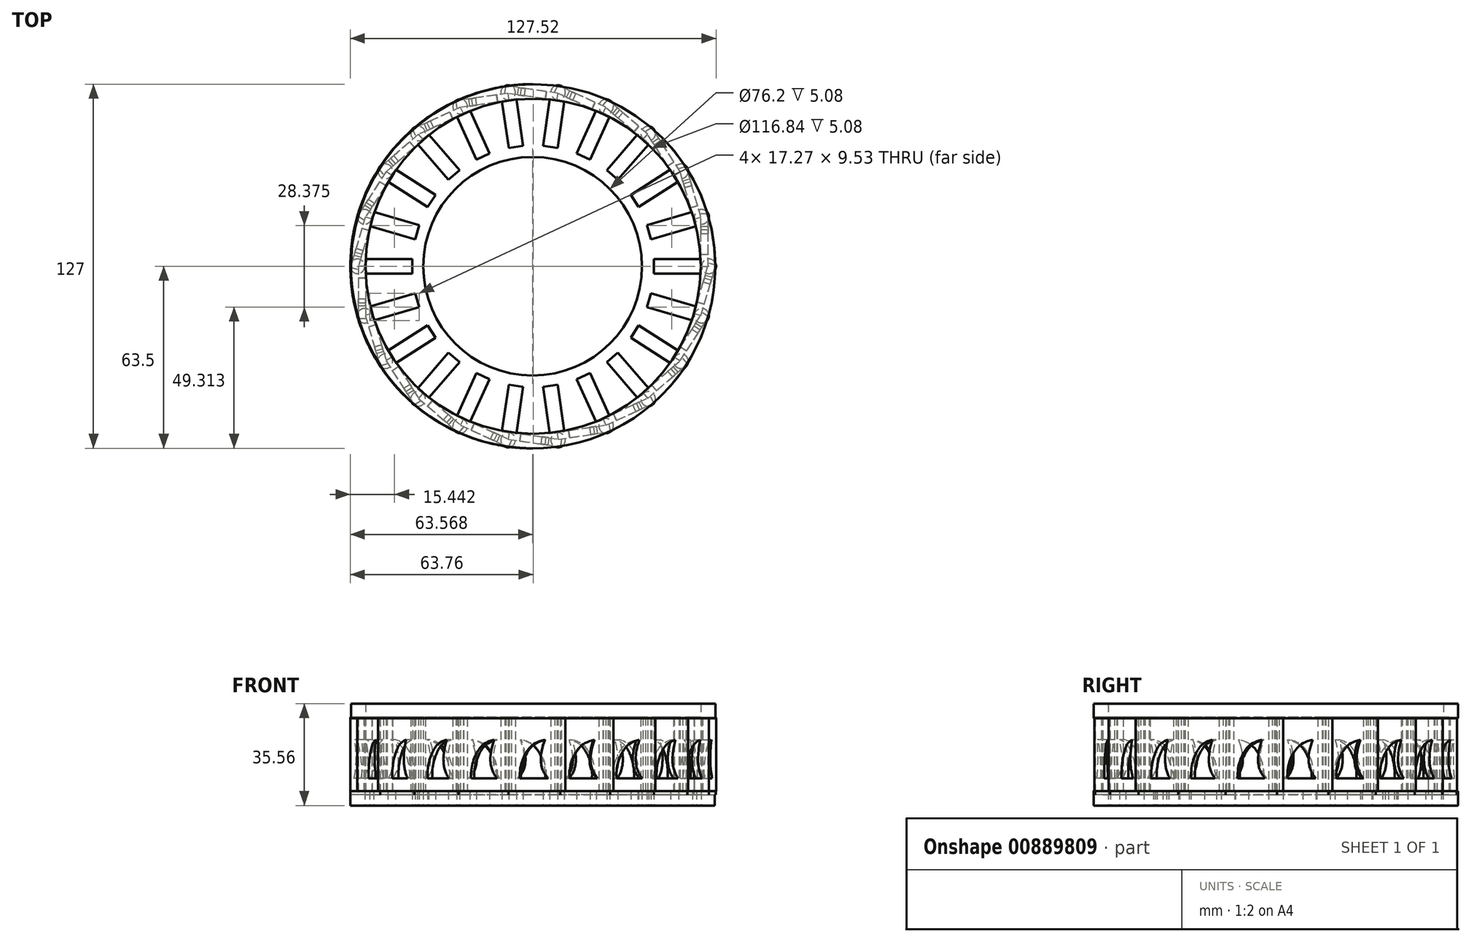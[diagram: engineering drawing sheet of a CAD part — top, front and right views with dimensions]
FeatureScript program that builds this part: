
annotation { "Feature Type Name" : "Feature", "Feature Type Description" : "" }
export const myFeature = defineFeature(function(context is Context, id is Id, definition is map)
    precondition{}
    {
        {
            var Q0;
            Q0=qCreatedBy(makeId("Top.planeOp"),FACE);
            var sketch = newSketch(context, id + "F0", { "sketchPlane" : qUnion([Q0])});
            skCircle(sketch, "E0", {"center": v(-0.2, 0) * mm, "radius": 38.1 * mm});
            skCircle(sketch, "E1", {"center": v(-0.2, 0) * mm, "radius": 63.5 * mm});
            skLineSegment(sketch, "E2.bottom", {"start": v(-58.61, 2.54) * mm, "end": v(-42.1, 2.54) * mm});
            skLineSegment(sketch, "E2.top", {"start": v(-58.61, -2.54) * mm, "end": v(-42.1, -2.54) * mm});
            skLineSegment(sketch, "E2.left", {"start": v(-58.61, 2.54) * mm, "end": v(-58.61, -2.54) * mm});
            skLineSegment(sketch, "E2.right", {"start": v(-42.1, 2.54) * mm, "end": v(-42.1, -2.54) * mm});
            skLineSegment(sketch, "E3.1.0", {"start": v(-41.11, -9.42) * mm, "end": v(-39.68, -14.3) * mm});
            skLineSegment(sketch, "E3.1.1", {"start": v(-56.95, -14.08) * mm, "end": v(-55.52, -18.95) * mm});
            skLineSegment(sketch, "E3.1.2", {"start": v(-55.52, -18.95) * mm, "end": v(-39.68, -14.3) * mm});
            skLineSegment(sketch, "E3.1.3", {"start": v(-56.95, -14.08) * mm, "end": v(-41.11, -9.42) * mm});
            skLineSegment(sketch, "E3.2.0", {"start": v(-36.8, -20.63) * mm, "end": v(-34.05, -24.9) * mm});
            skLineSegment(sketch, "E3.2.1", {"start": v(-50.68, -29.55) * mm, "end": v(-47.93, -33.83) * mm});
            skLineSegment(sketch, "E3.2.2", {"start": v(-47.93, -33.83) * mm, "end": v(-34.05, -24.9) * mm});
            skLineSegment(sketch, "E3.2.3", {"start": v(-50.68, -29.55) * mm, "end": v(-36.8, -20.63) * mm});
            skLineSegment(sketch, "E3.3.0", {"start": v(-29.5, -30.16) * mm, "end": v(-25.65, -33.48) * mm});
            skLineSegment(sketch, "E3.3.1", {"start": v(-40.3, -42.63) * mm, "end": v(-36.46, -45.96) * mm});
            skLineSegment(sketch, "E3.3.2", {"start": v(-36.46, -45.96) * mm, "end": v(-25.65, -33.48) * mm});
            skLineSegment(sketch, "E3.3.3", {"start": v(-40.3, -42.63) * mm, "end": v(-29.5, -30.16) * mm});
            skLineSegment(sketch, "E3.4.0", {"start": v(-19.8, -37.24) * mm, "end": v(-15.18, -39.35) * mm});
            skLineSegment(sketch, "E3.4.1", {"start": v(-26.66, -52.26) * mm, "end": v(-22.04, -54.37) * mm});
            skLineSegment(sketch, "E3.4.2", {"start": v(-22.04, -54.37) * mm, "end": v(-15.18, -39.35) * mm});
            skLineSegment(sketch, "E3.4.3", {"start": v(-26.66, -52.26) * mm, "end": v(-19.8, -37.24) * mm});
            skLineSegment(sketch, "E3.5.0", {"start": v(-8.5, -41.31) * mm, "end": v(-3.48, -42.04) * mm});
            skLineSegment(sketch, "E3.5.1", {"start": v(-10.86, -57.65) * mm, "end": v(-5.83, -58.38) * mm});
            skLineSegment(sketch, "E3.5.2", {"start": v(-5.83, -58.38) * mm, "end": v(-3.48, -42.04) * mm});
            skLineSegment(sketch, "E3.5.3", {"start": v(-10.86, -57.65) * mm, "end": v(-8.5, -41.31) * mm});
            skLineSegment(sketch, "E3.6.0", {"start": v(3.48, -42.04) * mm, "end": v(8.5, -41.31) * mm});
            skLineSegment(sketch, "E3.6.1", {"start": v(5.83, -58.38) * mm, "end": v(10.86, -57.65) * mm});
            skLineSegment(sketch, "E3.6.2", {"start": v(10.86, -57.65) * mm, "end": v(8.5, -41.31) * mm});
            skLineSegment(sketch, "E3.6.3", {"start": v(5.83, -58.38) * mm, "end": v(3.48, -42.04) * mm});
            skLineSegment(sketch, "E3.7.0", {"start": v(15.18, -39.35) * mm, "end": v(19.8, -37.24) * mm});
            skLineSegment(sketch, "E3.7.1", {"start": v(22.04, -54.37) * mm, "end": v(26.66, -52.26) * mm});
            skLineSegment(sketch, "E3.7.2", {"start": v(26.66, -52.26) * mm, "end": v(19.8, -37.24) * mm});
            skLineSegment(sketch, "E3.7.3", {"start": v(22.04, -54.37) * mm, "end": v(15.18, -39.35) * mm});
            skLineSegment(sketch, "E3.8.0", {"start": v(25.65, -33.48) * mm, "end": v(29.5, -30.16) * mm});
            skLineSegment(sketch, "E3.8.1", {"start": v(36.46, -45.96) * mm, "end": v(40.3, -42.63) * mm});
            skLineSegment(sketch, "E3.8.2", {"start": v(40.3, -42.63) * mm, "end": v(29.5, -30.16) * mm});
            skLineSegment(sketch, "E3.8.3", {"start": v(36.46, -45.96) * mm, "end": v(25.65, -33.48) * mm});
            skLineSegment(sketch, "E3.9.0", {"start": v(34.05, -24.9) * mm, "end": v(36.8, -20.63) * mm});
            skLineSegment(sketch, "E3.9.1", {"start": v(47.93, -33.83) * mm, "end": v(50.68, -29.55) * mm});
            skLineSegment(sketch, "E3.9.2", {"start": v(50.68, -29.55) * mm, "end": v(36.8, -20.63) * mm});
            skLineSegment(sketch, "E3.9.3", {"start": v(47.93, -33.83) * mm, "end": v(34.05, -24.9) * mm});
            skLineSegment(sketch, "E3.10.0", {"start": v(39.68, -14.3) * mm, "end": v(41.11, -9.42) * mm});
            skLineSegment(sketch, "E3.10.1", {"start": v(55.52, -18.95) * mm, "end": v(56.95, -14.08) * mm});
            skLineSegment(sketch, "E3.10.2", {"start": v(56.95, -14.08) * mm, "end": v(41.11, -9.42) * mm});
            skLineSegment(sketch, "E3.10.3", {"start": v(55.52, -18.95) * mm, "end": v(39.68, -14.3) * mm});
            skLineSegment(sketch, "E3.11.0", {"start": v(42.1, -2.54) * mm, "end": v(42.1, 2.54) * mm});
            skLineSegment(sketch, "E3.11.1", {"start": v(58.61, -2.54) * mm, "end": v(58.61, 2.54) * mm});
            skLineSegment(sketch, "E3.11.2", {"start": v(58.61, 2.54) * mm, "end": v(42.1, 2.54) * mm});
            skLineSegment(sketch, "E3.11.3", {"start": v(58.61, -2.54) * mm, "end": v(42.1, -2.54) * mm});
            skLineSegment(sketch, "E3.12.0", {"start": v(41.11, 9.42) * mm, "end": v(39.68, 14.3) * mm});
            skLineSegment(sketch, "E3.12.1", {"start": v(56.95, 14.08) * mm, "end": v(55.52, 18.95) * mm});
            skLineSegment(sketch, "E3.12.2", {"start": v(55.52, 18.95) * mm, "end": v(39.68, 14.3) * mm});
            skLineSegment(sketch, "E3.12.3", {"start": v(56.95, 14.08) * mm, "end": v(41.11, 9.42) * mm});
            skLineSegment(sketch, "E3.13.0", {"start": v(36.8, 20.63) * mm, "end": v(34.05, 24.9) * mm});
            skLineSegment(sketch, "E3.13.1", {"start": v(50.68, 29.55) * mm, "end": v(47.93, 33.83) * mm});
            skLineSegment(sketch, "E3.13.2", {"start": v(47.93, 33.83) * mm, "end": v(34.05, 24.9) * mm});
            skLineSegment(sketch, "E3.13.3", {"start": v(50.68, 29.55) * mm, "end": v(36.8, 20.63) * mm});
            skLineSegment(sketch, "E3.14.0", {"start": v(29.5, 30.16) * mm, "end": v(25.65, 33.48) * mm});
            skLineSegment(sketch, "E3.14.1", {"start": v(40.3, 42.63) * mm, "end": v(36.46, 45.96) * mm});
            skLineSegment(sketch, "E3.14.2", {"start": v(36.46, 45.96) * mm, "end": v(25.65, 33.48) * mm});
            skLineSegment(sketch, "E3.14.3", {"start": v(40.3, 42.63) * mm, "end": v(29.5, 30.16) * mm});
            skLineSegment(sketch, "E3.15.0", {"start": v(19.8, 37.24) * mm, "end": v(15.18, 39.35) * mm});
            skLineSegment(sketch, "E3.15.1", {"start": v(26.66, 52.26) * mm, "end": v(22.04, 54.37) * mm});
            skLineSegment(sketch, "E3.15.2", {"start": v(22.04, 54.37) * mm, "end": v(15.18, 39.35) * mm});
            skLineSegment(sketch, "E3.15.3", {"start": v(26.66, 52.26) * mm, "end": v(19.8, 37.24) * mm});
            skLineSegment(sketch, "E3.16.0", {"start": v(8.5, 41.31) * mm, "end": v(3.48, 42.04) * mm});
            skLineSegment(sketch, "E3.16.1", {"start": v(10.86, 57.65) * mm, "end": v(5.83, 58.38) * mm});
            skLineSegment(sketch, "E3.16.2", {"start": v(5.83, 58.38) * mm, "end": v(3.48, 42.04) * mm});
            skLineSegment(sketch, "E3.16.3", {"start": v(10.86, 57.65) * mm, "end": v(8.5, 41.31) * mm});
            skLineSegment(sketch, "E3.17.0", {"start": v(-3.48, 42.04) * mm, "end": v(-8.5, 41.31) * mm});
            skLineSegment(sketch, "E3.17.1", {"start": v(-5.83, 58.38) * mm, "end": v(-10.86, 57.65) * mm});
            skLineSegment(sketch, "E3.17.2", {"start": v(-10.86, 57.65) * mm, "end": v(-8.5, 41.31) * mm});
            skLineSegment(sketch, "E3.17.3", {"start": v(-5.83, 58.38) * mm, "end": v(-3.48, 42.04) * mm});
            skLineSegment(sketch, "E3.18.0", {"start": v(-15.18, 39.35) * mm, "end": v(-19.8, 37.24) * mm});
            skLineSegment(sketch, "E3.18.1", {"start": v(-22.04, 54.37) * mm, "end": v(-26.66, 52.26) * mm});
            skLineSegment(sketch, "E3.18.2", {"start": v(-26.66, 52.26) * mm, "end": v(-19.8, 37.24) * mm});
            skLineSegment(sketch, "E3.18.3", {"start": v(-22.04, 54.37) * mm, "end": v(-15.18, 39.35) * mm});
            skLineSegment(sketch, "E3.19.0", {"start": v(-25.65, 33.48) * mm, "end": v(-29.5, 30.16) * mm});
            skLineSegment(sketch, "E3.19.1", {"start": v(-36.46, 45.96) * mm, "end": v(-40.3, 42.63) * mm});
            skLineSegment(sketch, "E3.19.2", {"start": v(-40.3, 42.63) * mm, "end": v(-29.5, 30.16) * mm});
            skLineSegment(sketch, "E3.19.3", {"start": v(-36.46, 45.96) * mm, "end": v(-25.65, 33.48) * mm});
            skLineSegment(sketch, "E3.20.0", {"start": v(-34.05, 24.9) * mm, "end": v(-36.8, 20.63) * mm});
            skLineSegment(sketch, "E3.20.1", {"start": v(-47.93, 33.83) * mm, "end": v(-50.68, 29.55) * mm});
            skLineSegment(sketch, "E3.20.2", {"start": v(-50.68, 29.55) * mm, "end": v(-36.8, 20.63) * mm});
            skLineSegment(sketch, "E3.20.3", {"start": v(-47.93, 33.83) * mm, "end": v(-34.05, 24.9) * mm});
            skLineSegment(sketch, "E3.21.0", {"start": v(-39.68, 14.3) * mm, "end": v(-41.11, 9.42) * mm});
            skLineSegment(sketch, "E3.21.1", {"start": v(-55.52, 18.95) * mm, "end": v(-56.95, 14.08) * mm});
            skLineSegment(sketch, "E3.21.2", {"start": v(-56.95, 14.08) * mm, "end": v(-41.11, 9.42) * mm});
            skLineSegment(sketch, "E3.21.3", {"start": v(-55.52, 18.95) * mm, "end": v(-39.68, 14.3) * mm});
            skPoint(sketch, "E3.center", {"position": v(0, 0) * mm});
            skSolve(sketch);
        }
        {
            var Q0;
            Q0=makeQuery(id+"F0.imprint","IMPRINT",FACE,{"disambiguationData":[TD([[makeQuery(id+"F0.imprint","IMPRINT",EDGE,{"derivedFrom":sQuery(id+"F0.wireOp",EDGE,"E0")}),-1.0]])]});
            extrude(context, id + "F1", {"entities" : qUnion([Q0]), "depth" : 5.08 * mm, "offsetDistance" : 25.4 * mm});
        }
        {
            var Q0;
            Q0=makeQuery(id+"F1.opExtrude","CAP_FACE",FACE,{"disambiguationData":[OSD([sQuery(id+"F0.wireOp",EDGE,"E0"),sQuery(id+"F0.wireOp",EDGE,"E1"),sQuery(id+"F0.wireOp",EDGE,"E2.bottom"),sQuery(id+"F0.wireOp",EDGE,"E2.top"),sQuery(id+"F0.wireOp",EDGE,"E2.left"),sQuery(id+"F0.wireOp",EDGE,"E2.right"),sQuery(id+"F0.wireOp",EDGE,"E3.1.0"),sQuery(id+"F0.wireOp",EDGE,"E3.1.1"),sQuery(id+"F0.wireOp",EDGE,"E3.1.2"),sQuery(id+"F0.wireOp",EDGE,"E3.1.3"),sQuery(id+"F0.wireOp",EDGE,"E3.2.0"),sQuery(id+"F0.wireOp",EDGE,"E3.2.1"),sQuery(id+"F0.wireOp",EDGE,"E3.2.2"),sQuery(id+"F0.wireOp",EDGE,"E3.2.3"),sQuery(id+"F0.wireOp",EDGE,"E3.3.0"),sQuery(id+"F0.wireOp",EDGE,"E3.3.1"),sQuery(id+"F0.wireOp",EDGE,"E3.3.2"),sQuery(id+"F0.wireOp",EDGE,"E3.3.3"),sQuery(id+"F0.wireOp",EDGE,"E3.4.0"),sQuery(id+"F0.wireOp",EDGE,"E3.4.1"),sQuery(id+"F0.wireOp",EDGE,"E3.4.2"),sQuery(id+"F0.wireOp",EDGE,"E3.4.3"),sQuery(id+"F0.wireOp",EDGE,"E3.5.0"),sQuery(id+"F0.wireOp",EDGE,"E3.5.1"),sQuery(id+"F0.wireOp",EDGE,"E3.5.2"),sQuery(id+"F0.wireOp",EDGE,"E3.5.3"),sQuery(id+"F0.wireOp",EDGE,"E3.6.0"),sQuery(id+"F0.wireOp",EDGE,"E3.6.1"),sQuery(id+"F0.wireOp",EDGE,"E3.6.2"),sQuery(id+"F0.wireOp",EDGE,"E3.6.3"),sQuery(id+"F0.wireOp",EDGE,"E3.7.0"),sQuery(id+"F0.wireOp",EDGE,"E3.7.1"),sQuery(id+"F0.wireOp",EDGE,"E3.7.2"),sQuery(id+"F0.wireOp",EDGE,"E3.7.3"),sQuery(id+"F0.wireOp",EDGE,"E3.8.0"),sQuery(id+"F0.wireOp",EDGE,"E3.8.1"),sQuery(id+"F0.wireOp",EDGE,"E3.8.2"),sQuery(id+"F0.wireOp",EDGE,"E3.8.3"),sQuery(id+"F0.wireOp",EDGE,"E3.9.0"),sQuery(id+"F0.wireOp",EDGE,"E3.9.1"),sQuery(id+"F0.wireOp",EDGE,"E3.9.2"),sQuery(id+"F0.wireOp",EDGE,"E3.9.3"),sQuery(id+"F0.wireOp",EDGE,"E3.10.0"),sQuery(id+"F0.wireOp",EDGE,"E3.10.1"),sQuery(id+"F0.wireOp",EDGE,"E3.10.2"),sQuery(id+"F0.wireOp",EDGE,"E3.10.3"),sQuery(id+"F0.wireOp",EDGE,"E3.11.0"),sQuery(id+"F0.wireOp",EDGE,"E3.11.1"),sQuery(id+"F0.wireOp",EDGE,"E3.11.2"),sQuery(id+"F0.wireOp",EDGE,"E3.11.3"),sQuery(id+"F0.wireOp",EDGE,"E3.12.0"),sQuery(id+"F0.wireOp",EDGE,"E3.12.1"),sQuery(id+"F0.wireOp",EDGE,"E3.12.2"),sQuery(id+"F0.wireOp",EDGE,"E3.12.3"),sQuery(id+"F0.wireOp",EDGE,"E3.13.0"),sQuery(id+"F0.wireOp",EDGE,"E3.13.1"),sQuery(id+"F0.wireOp",EDGE,"E3.13.2"),sQuery(id+"F0.wireOp",EDGE,"E3.13.3"),sQuery(id+"F0.wireOp",EDGE,"E3.14.0"),sQuery(id+"F0.wireOp",EDGE,"E3.14.1"),sQuery(id+"F0.wireOp",EDGE,"E3.14.2"),sQuery(id+"F0.wireOp",EDGE,"E3.14.3"),sQuery(id+"F0.wireOp",EDGE,"E3.15.0"),sQuery(id+"F0.wireOp",EDGE,"E3.15.1"),sQuery(id+"F0.wireOp",EDGE,"E3.15.2"),sQuery(id+"F0.wireOp",EDGE,"E3.15.3"),sQuery(id+"F0.wireOp",EDGE,"E3.16.0"),sQuery(id+"F0.wireOp",EDGE,"E3.16.1"),sQuery(id+"F0.wireOp",EDGE,"E3.16.2"),sQuery(id+"F0.wireOp",EDGE,"E3.16.3"),sQuery(id+"F0.wireOp",EDGE,"E3.17.0"),sQuery(id+"F0.wireOp",EDGE,"E3.17.1"),sQuery(id+"F0.wireOp",EDGE,"E3.17.2"),sQuery(id+"F0.wireOp",EDGE,"E3.17.3"),sQuery(id+"F0.wireOp",EDGE,"E3.18.0"),sQuery(id+"F0.wireOp",EDGE,"E3.18.1"),sQuery(id+"F0.wireOp",EDGE,"E3.18.2"),sQuery(id+"F0.wireOp",EDGE,"E3.18.3"),sQuery(id+"F0.wireOp",EDGE,"E3.19.0"),sQuery(id+"F0.wireOp",EDGE,"E3.19.1"),sQuery(id+"F0.wireOp",EDGE,"E3.19.2"),sQuery(id+"F0.wireOp",EDGE,"E3.19.3"),sQuery(id+"F0.wireOp",EDGE,"E3.20.0"),sQuery(id+"F0.wireOp",EDGE,"E3.20.1"),sQuery(id+"F0.wireOp",EDGE,"E3.20.2"),sQuery(id+"F0.wireOp",EDGE,"E3.20.3"),sQuery(id+"F0.wireOp",EDGE,"E3.21.0"),sQuery(id+"F0.wireOp",EDGE,"E3.21.1"),sQuery(id+"F0.wireOp",EDGE,"E3.21.2"),sQuery(id+"F0.wireOp",EDGE,"E3.21.3")])],"isStart":false});
            var sketch = newSketch(context, id + "F2", { "sketchPlane" : qUnion([Q0])});
            skCircle(sketch, "E4", {"center": v(-61.22, 0) * mm, "radius": 2.54 * mm});
            skCircle(sketch, "E5.1.0", {"center": v(-58.74, -17.25) * mm, "radius": 2.54 * mm});
            skCircle(sketch, "E5.2.0", {"center": v(-51.5, -33.1) * mm, "radius": 2.54 * mm});
            skCircle(sketch, "E5.3.0", {"center": v(-40.09, -46.27) * mm, "radius": 2.54 * mm});
            skCircle(sketch, "E5.4.0", {"center": v(-25.43, -55.69) * mm, "radius": 2.54 * mm});
            skCircle(sketch, "E5.5.0", {"center": v(-8.71, -60.6) * mm, "radius": 2.54 * mm});
            skCircle(sketch, "E5.6.0", {"center": v(8.71, -60.6) * mm, "radius": 2.54 * mm});
            skCircle(sketch, "E5.7.0", {"center": v(25.43, -55.69) * mm, "radius": 2.54 * mm});
            skCircle(sketch, "E5.8.0", {"center": v(40.09, -46.27) * mm, "radius": 2.54 * mm});
            skCircle(sketch, "E5.9.0", {"center": v(51.5, -33.1) * mm, "radius": 2.54 * mm});
            skCircle(sketch, "E5.10.0", {"center": v(58.74, -17.25) * mm, "radius": 2.54 * mm});
            skCircle(sketch, "E5.11.0", {"center": v(61.22, 0) * mm, "radius": 2.54 * mm});
            skCircle(sketch, "E5.12.0", {"center": v(58.74, 17.25) * mm, "radius": 2.54 * mm});
            skCircle(sketch, "E5.13.0", {"center": v(51.5, 33.1) * mm, "radius": 2.54 * mm});
            skCircle(sketch, "E5.14.0", {"center": v(40.09, 46.27) * mm, "radius": 2.54 * mm});
            skCircle(sketch, "E5.15.0", {"center": v(25.43, 55.69) * mm, "radius": 2.54 * mm});
            skCircle(sketch, "E5.16.0", {"center": v(8.71, 60.6) * mm, "radius": 2.54 * mm});
            skCircle(sketch, "E5.17.0", {"center": v(-8.71, 60.6) * mm, "radius": 2.54 * mm});
            skCircle(sketch, "E5.18.0", {"center": v(-25.43, 55.69) * mm, "radius": 2.54 * mm});
            skCircle(sketch, "E5.19.0", {"center": v(-40.09, 46.27) * mm, "radius": 2.54 * mm});
            skCircle(sketch, "E5.20.0", {"center": v(-51.5, 33.1) * mm, "radius": 2.54 * mm});
            skCircle(sketch, "E5.21.0", {"center": v(-58.74, 17.25) * mm, "radius": 2.54 * mm});
            skPoint(sketch, "E5.center", {"position": v(0, 0) * mm});
            skSolve(sketch);
        }
        {
            var Q0;
            Q0 = qSketchRegion(id + "F2", true);
            extrude(context, id + "F3", {"entities" : qUnion([Q0]), "operationType" : NewBodyOperationType.ADD, "depth" : 25.4 * mm, "offsetDistance" : 25.4 * mm});
        }
        {
            var Q0;
            Q0=makeQuery(id+"F3.opExtrude","CAP_FACE",FACE,{"disambiguationData":[OSD([sQuery(id+"F2.wireOp",EDGE,"E4")])],"isStart":false});
            var sketch = newSketch(context, id + "F4", { "sketchPlane" : qUnion([Q0])});
            skCircle(sketch, "E6", {"center": v(0, 0) * mm, "radius": 63.5 * mm});
            skCircle(sketch, "E7", {"center": v(0, 0) * mm, "radius": 58.42 * mm});
            skSolve(sketch);
        }
        {
            var Q0;
            Q0 = qSketchRegion(id + "F4", true);
            extrude(context, id + "F5", {"entities" : qUnion([Q0]), "operationType" : NewBodyOperationType.ADD, "depth" : 5.08 * mm, "offsetDistance" : 25.4 * mm});
        }
        {
            var Q0;
            Q0=qCreatedBy(makeId("Right.planeOp"),FACE);
            cPlane(context, id + "F6", {"entities" : qUnion([Q0]), "cplaneType" : CPlaneType.OFFSET, "offset" : 60.96 * mm, "width" : 152.4 * mm, "height" : 152.4 * mm});
        }
        {
            var Q0;
            Q0=qCreatedBy(id+"F6.planeOp",FACE);
            var sketch = newSketch(context, id + "F7", { "sketchPlane" : qUnion([Q0])});
            skLineSegment(sketch, "E8", {"start": v(4.12, 9.54) * mm, "end": v(13.9, 9.54) * mm});
            skLineSegment(sketch, "E9.bottom", {"start": v(0, 30.84) * mm, "end": v(18.36, 30.84) * mm});
            skLineSegment(sketch, "E9.top", {"start": v(0, 3.76) * mm, "end": v(18.36, 3.76) * mm});
            skLineSegment(sketch, "E9.left", {"start": v(0, 30.84) * mm, "end": v(0, 3.76) * mm});
            skLineSegment(sketch, "E9.right", {"start": v(18.36, 30.84) * mm, "end": v(18.36, 3.76) * mm});
            skFitSpline(sketch, "E10", {"points": [v(13.9, 9.54) * mm, v(11.92, 13.02) * mm, v(12.85, 22.88) * mm], "startDerivative": vector(-7.6, 9.94) * mm, "endDerivative": vector(8.76, 24.28) * mm});
            skFitSpline(sketch, "E11", {"points": [v(4.12, 9.54) * mm, v(6.24, 18.4) * mm, v(12.85, 22.88) * mm], "startDerivative": vector(-1.74, 21.13) * mm, "endDerivative": vector(23.32, 4.5) * mm});
            skSolve(sketch);
        }
        {
            var Q0;
            Q0 = qSketchRegion(id + "F7", true);
            extrude(context, id + "F8", {"entities" : qUnion([Q0]), "depth" : -2.54 * mm, "offsetDistance" : 25.4 * mm});
        }
        {
            var Q0;
            Q0=qCreatedBy(makeId("Right.planeOp"),FACE);
            var sketch = newSketch(context, id + "F9", { "sketchPlane" : qUnion([Q0])});
            skLineSegment(sketch, "E12", {"start": v(0, 63.76) * mm, "end": v(0, 0) * mm, "construction": true});
            skSolve(sketch);
        }
        {
            var Q0;
            Q0=makeQuery(id+"F8.opExtrude","SWEPT_BODY",BODY,{"disambiguationData":[OSD([sQuery(id+"F7.wireOp",EDGE,"E8"),sQuery(id+"F7.wireOp",EDGE,"48475a9f-e03c-40e3-8c9d-36d22738f227")])]});
            var Q1;
            Q1=sQuery(id+"F9.wireOp",EDGE,"E12");
            circularPattern(context, id + "F10", {"entities" : qUnion([Q0]), "axis" : qUnion([Q1]), "angle" : 360 * degree, "instanceCount" : 22, "equalSpace" : true});
        }
    });
